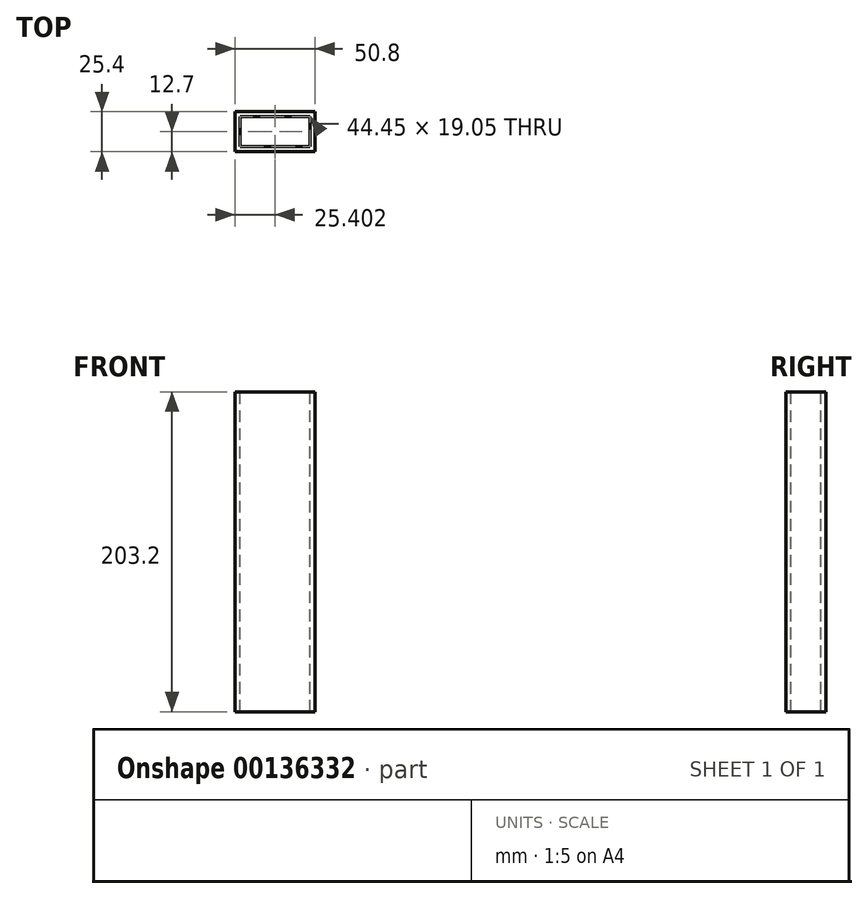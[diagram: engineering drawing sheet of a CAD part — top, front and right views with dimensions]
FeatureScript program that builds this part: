
annotation { "Feature Type Name" : "Feature", "Feature Type Description" : "" }
export const myFeature = defineFeature(function(context is Context, id is Id, definition is map)
    precondition{}
    {
        {
            var Q0;
            Q0=qCreatedBy(makeId("Front.planeOp"),FACE);
            var sketch = newSketch(context, id + "F0", { "sketchPlane" : qUnion([Q0])});
            skLineSegment(sketch, "E0.bottom", {"start": v(-136.6, 0) * mm, "end": v(-85.8, 0) * mm});
            skLineSegment(sketch, "E0.top", {"start": v(-136.6, 203.2) * mm, "end": v(-85.8, 203.2) * mm});
            skLineSegment(sketch, "E0.left", {"start": v(-136.6, 0) * mm, "end": v(-136.6, 203.2) * mm});
            skLineSegment(sketch, "E0.right", {"start": v(-85.8, 0) * mm, "end": v(-85.8, 203.2) * mm});
            skSolve(sketch);
        }
        {
            var Q0;
            Q0 = qSketchRegion(id + "F0", true);
            extrude(context, id + "F1", {"entities" : qUnion([Q0]), "depth" : 25.4 * mm});
        }
        {
            var Q0;
            Q0=makeQuery(id+"F1.opExtrude","SWEPT_FACE",FACE,{"disambiguationData":[OSD([sQuery(id+"F0.wireOp",EDGE,"E0.top")])]});
            var Q1;
            Q1=makeQuery(id+"F1.opExtrude","SWEPT_FACE",FACE,{"disambiguationData":[OSD([sQuery(id+"F0.wireOp",EDGE,"E0.bottom")])]});
            shell(context, id + "F2", {"entities" : qUnion([Q0, Q1]), "thickness" : 3.17 * mm});
        }
    });
